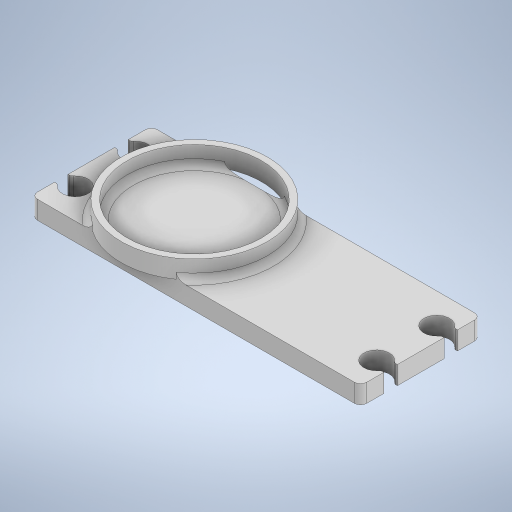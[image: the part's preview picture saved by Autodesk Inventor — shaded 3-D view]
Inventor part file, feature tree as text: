
AUTODESK INVENTOR PART (.ipt)
format: ipt  version: 2024 (Build 280153000, 153)  size: 752,128 bytes
history: native  units: mm
features: other x5, reference x4, extrude x2, fillet x2, sketch x2, plane x1
ambient origin geometry x8: Origin, YZ Plane, XZ Plane, XY Plane, X Axis, Y Axis, Z Axis, Center Point
bodies: Solid1 (feature_tree)
feature tree (16):
  extrude  "Extrusion1"  Depth=1.0mm
  plane  "Work Plane1"
  extrude  "Extrusion2"  Depth=1.0mm TaperAngle=0.0deg
  fillet  "Fillet1"  Radius=1.0mm
  fillet  "Fillet2"  Radius=1.0mm
  sketch  "Sketch1"  dims[d0=24.0mm d1=1.0mm]
  reference  "Reference1"
  reference  "Reference2"
  sketch  "Sketch2"  dims[d2=3.0mm d3=0.0mm d4=3.0mm d5=0.0mm d6=1.0mm d7=1.0mm]
  reference  "Reference3"
  reference  "Reference4"
  other  "<userpath> windows\Documents\Inventor\Robotska_roka\roka.iam"
  other  "roka.iam"
  other  "Servo Motor MG996R  With Attachments:7"
  other  "servoMotorMG996R_7"
  other  "servoMotorMG996R_6"
